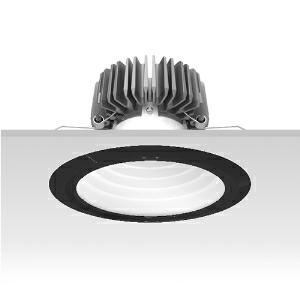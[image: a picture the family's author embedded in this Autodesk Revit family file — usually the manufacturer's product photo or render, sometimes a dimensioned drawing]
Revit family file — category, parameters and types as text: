
# Revit family: 3f_filippi_-_3f_reno_bianco_ampio_3f_filippi_-_30671_a01026_-_3f_reno_200_wh_2000-840_dali_wide___vt_bk_649e
name_source: partatom
category: Lighting Fixtures
units: mm (PartAtom-declared; Revit-internal decimal feet)

## family parameters
Cut with Voids When Loaded = No
Host = Face
Light Source = No
Part Type = Normal
Room Calculation Point = No
Round Connector Dimension = Use Diameter
Shared = No

## types (1)
- 3F Filippi - 3F Reno Bianco Ampio (1 x LED, 1884 lm, 20 W, 4000 K)
    Apparent Load = 20 VA
    Approval mark = CE
    CIE Flux Codes = 75 94 99 100 100
    Color Rendering = 80
    Color Temperature = 4000 K
    Control Gear = Electronic transformer
    Default Elevation = 1800 mm
    Description = ILLUMINOTECHNICAL
Luminous efficiency 100% (DLOR 100%, ULOR 0%).
Initial luminous flux of the luminaire 1884 lm.
Direct symmetric wide distribution.
Installation Interdistance Transv.D = 1.56 x hu - Long.D = 1.56 x hu.
Average luminance <3000 cd/m² for radial angles >65°.
Tabular UGR (CIE 117 - 4H-8H; S=0.25H; 70/50/20): RUG 20.8 - 20.6.
Beam angle: 74° - 74°.
Luminous efficacy 94 lm/W.
Lifetime (L90/B10): 30000 h. (tq+25°C)
Lifetime (L85/B10): 50000 h. (tq+25°C)
Lifetime (L70/B10): 80000 h. (tq+25°C)
Sudden decreased luminous flux after 50000 hours: 0% (C0).
Photobiological safety in compliance with IEC/TR 62778: RG0 risk exempt, (IEC 62471).
In compliance with IEC/EN 62722-2-1 - IEC/EN 62717 standards.

SOURCE
Compact LED module 2000/840.
Energy efficiency class (UE 2019/2020 - UE 2019/2015): D.
CIE 13.3 Colour rendering index: CRI >80 (R9 <50%).
IES TM-30 Fidelity Index: Rf = 84 Rg = 95.
CCT nominal colour temperature 4000 K.
Colour initial tolerance (MacAdam): SDCM 3.
Zhaga Book 3 compliant.

MECHANICAL
Passive heat dissipator in die-casting aluminium, oversized, for optimum thermal management of the LED module.
Parabolic element with graduated/concentric rings in white polycarbonate.
Transparent external lens with glossy and satin differentiated surfaces, with a cooling and anti-insect system in methacrylate (PMMA).
Fastening spring clips in stainless steel.
Dimensions: diameter 226 mm, height 146 mm. Weight 1.16 kg.
IP44 protection degree for exposed part, IP20 for recessed part.
Mechanical strength to impacts IK06 (1 joule).
Glow-wire test resistance 650°C.

ELECTRICAL
Wiring on a separate unit.
Halogen Free DALI-2 DATI (Parts 251, 252, 253), PUSH-DIM, electronic wiring 230V-50/60Hz, power factor 0.90 at full load, THD <25%, constant output current, SELV, class II, 1 driver, 1 DALI addresse.
Power of the luminaire 20 W.
ENEC - CE.
SAFE FLICKER: PstLM=<1 and SVM=<0.4 (IEC TR 61547-1 and IEC TR 63158), to ensure a more comfortable and safe light.
Luminaire compliant with EN 60598-2-22 for power supply from a centralised emergency system CPSS (Central Power Supply System), not incorporated in the luminaire - high risk areas excluded. The default power and flux are 100% in AC and 100% in DC.
Ambient temperature from 0°C to +25°C.
Temperature class T6 max 85°C.
Relative humidity UR: <85%.

INSTALLATION
Pull-up recessed fitting.
False ceiling carving: 200 mm.
All accessories dedicated to this product are available on the Catalog and on our website www.3F-Filippi.com.

ACCESSORIES
A01026 - VT transparent glass, tempered, not flammable, locked and in line with the trim, in black polycarbonate.

APPLICATIONS
Environments: architectural, commercial, exhibition areas, transit areas, corridors, shops, display windows, service areas.
In false ceilings with narrow voids.

LIGHT MANAGEMENT
Recommended minimum setting: 10%.
The luminaire, equipped with (DALI-2 DATI) driver, can be controlled manually with 3F Easy Dim technology or automatically/manually with wired or wireless DALI/D2D control systems.
The D2D driver guarantees interoperability with other devices with the same certification by making the following information available:
Device Data (Part 251), Energy Report (Part 252), Diagnosis & Maintenance (Part 253).
In electrical systems without a regulation system (manual or automatic) and DALI bus, a suitable jumper must be made on the DA-DA terminals of the appliance.

WARNING
Luminaire designed for disposal/recycling at end-of-life.
Replaceable (LED only) light source by a professional. Replaceable control gear by a professional.
    Height = 0 mm  [stored 0 ft]
    Lamp = 1 x LED
    Lamp Light Flux = 1884 lm
    Lamp Power = 20 W
    Lamp count = 1
    Length = 226 mm
    Lifetime = 50000 h
    Luminous efficacy = 94 lm/W
    Manufacturer = 3F Filippi
    ModVariant = No
    Model = 3F Filippi - 30671+A01026 - 3F Reno 200 WH 2000-840 DALI WIDE + VT BK
    Mounting Place = Ceiling
    Mounting Type = Recessed
    Number of Poles = 1
    OnlyDefault = Yes
    Power Factor = 1
    Product Name = 3F Filippi - 3F Reno Bianco Ampio
    Product group = recessed luminaire
    ProductGroupID = 4
    Protection Class = Protection class II
    Protection Degree = IP 20
    RLX_Detail_Level = 1
    RLX_Emergency_Light_Flux = 0 lm
    RLX_Emergency_Type = 0
    RLX_Emergency_Type_DB = No
    RlxData = <blob elided: 102701 chars, md5=f81df751>
    Socket = socket
    Standby Power = 0 W
    System Light Flux = 1884 lm
    System Power = 20 W
    Type Comments = Product without accessories
    Type Image = 3ffilippi_3f_reno_200_wh__a01026.jpg
    URL = http://relux.com
    VarID = ---
    Voltage = 0 V
    Weight = 0.00 kg
    Width = 0 mm  [stored 0 ft]

note: [stored X ft] marks values corroborated as IEEE doubles in the binary element streams (Revit-internal decimal feet)

## geometry (parser evidence)
native form markers: Blend x4, Sweep x10
no freeform markers — native parametric forms only
